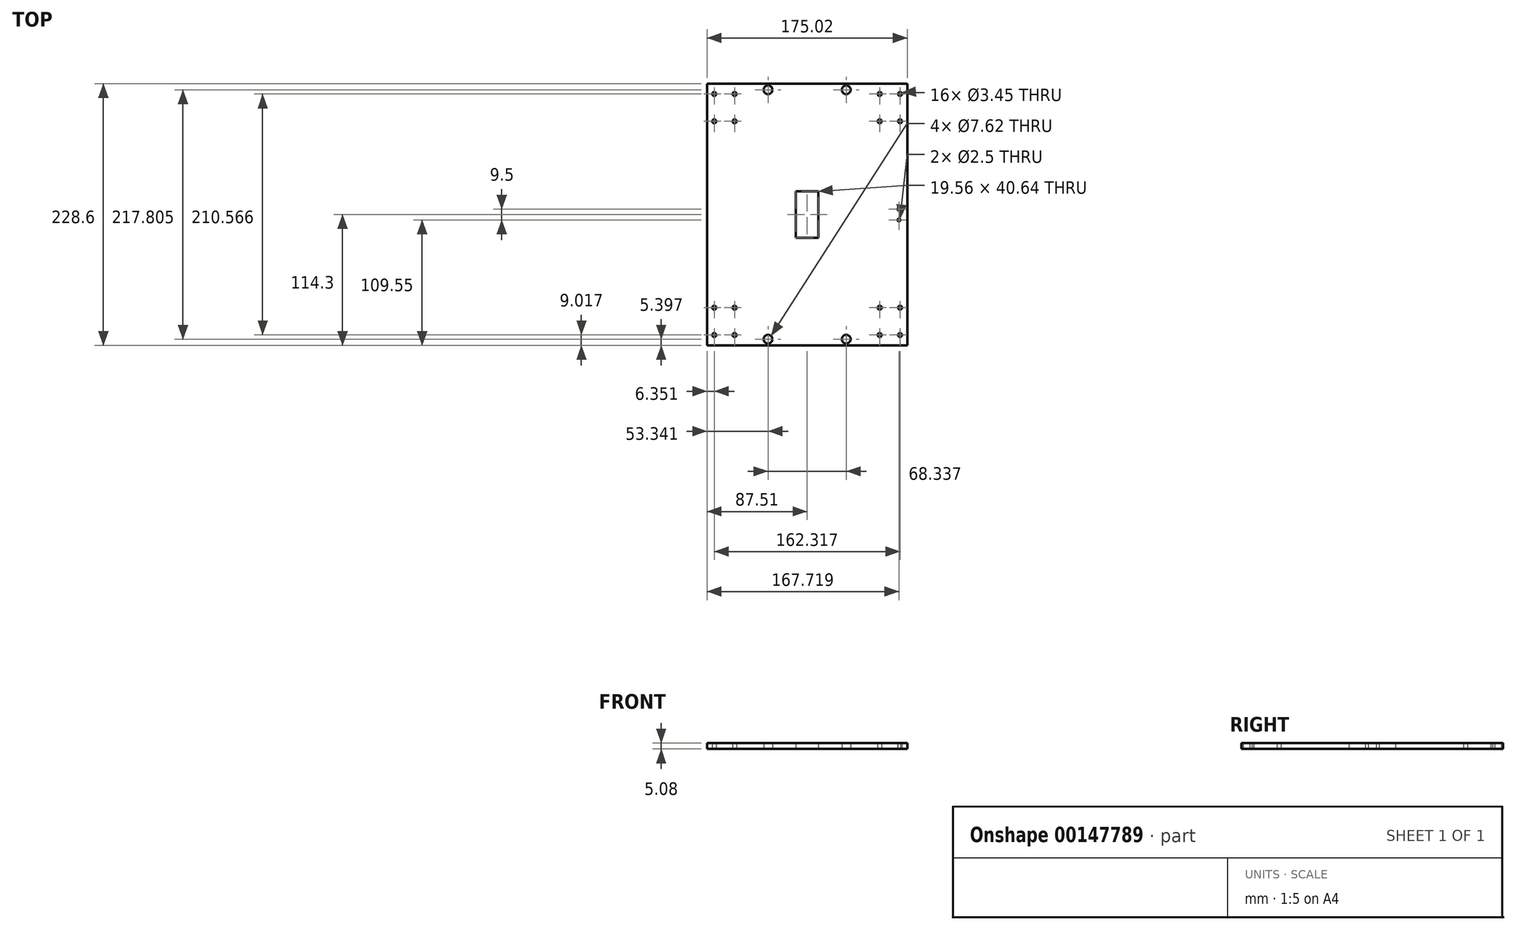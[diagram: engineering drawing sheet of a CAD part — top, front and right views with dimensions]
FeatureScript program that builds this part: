
annotation { "Feature Type Name" : "Feature", "Feature Type Description" : "" }
export const myFeature = defineFeature(function(context is Context, id is Id, definition is map)
    precondition{}
    {
        {
            var Q0;
            Q0=qCreatedBy(makeId("Top.planeOp"),FACE);
            var sketch = newSketch(context, id + "F0", { "sketchPlane" : qUnion([Q0])});
            skLineSegment(sketch, "E0.bottom", {"start": v(87.5, -114.3) * mm, "end": v(-87.5, -114.3) * mm});
            skLineSegment(sketch, "E0.top", {"start": v(87.5, 114.3) * mm, "end": v(-87.5, 114.3) * mm});
            skLineSegment(sketch, "E0.left", {"start": v(87.5, -114.3) * mm, "end": v(87.5, 114.3) * mm});
            skLineSegment(sketch, "E0.right", {"start": v(-87.5, -114.3) * mm, "end": v(-87.5, 114.3) * mm});
            skPoint(sketch, "E0.middle", {"position": v(0, 0) * mm});
            skLineSegment(sketch, "E1", {"start": v(-81.16, 114.3) * mm, "end": v(-81.16, 105.28) * mm, "construction": true});
            skLineSegment(sketch, "E2", {"start": v(-81.16, 105.28) * mm, "end": v(-87.5, 105.28) * mm, "construction": true});
            skLineSegment(sketch, "E3.bottom", {"start": v(-72.27, 93.34) * mm, "end": v(72.27, 93.34) * mm, "construction": true});
            skLineSegment(sketch, "E3.top", {"start": v(-72.27, -93.34) * mm, "end": v(72.27, -93.34) * mm, "construction": true});
            skLineSegment(sketch, "E3.left", {"start": v(-72.27, 93.34) * mm, "end": v(-72.27, -93.34) * mm, "construction": true});
            skLineSegment(sketch, "E3.right", {"start": v(72.27, 93.34) * mm, "end": v(72.27, -93.34) * mm, "construction": true});
            skLineSegment(sketch, "E4.bottom", {"start": v(-81.16, 105.28) * mm, "end": v(-63.38, 105.28) * mm, "construction": true});
            skLineSegment(sketch, "E4.top", {"start": v(-81.16, 81.4) * mm, "end": v(-63.38, 81.4) * mm, "construction": true});
            skLineSegment(sketch, "E4.left", {"start": v(-81.16, 105.28) * mm, "end": v(-81.16, 81.4) * mm, "construction": true});
            skLineSegment(sketch, "E4.right", {"start": v(-63.38, 105.28) * mm, "end": v(-63.38, 81.4) * mm, "construction": true});
            skPoint(sketch, "E4.middle", {"position": v(-72.27, 93.34) * mm});
            skLineSegment(sketch, "E5.bottom", {"start": v(81.16, 105.28) * mm, "end": v(63.38, 105.28) * mm, "construction": true});
            skLineSegment(sketch, "E5.top", {"start": v(81.16, 81.4) * mm, "end": v(63.38, 81.4) * mm, "construction": true});
            skLineSegment(sketch, "E5.left", {"start": v(81.16, 105.28) * mm, "end": v(81.16, 81.4) * mm, "construction": true});
            skLineSegment(sketch, "E5.right", {"start": v(63.38, 105.28) * mm, "end": v(63.38, 81.4) * mm, "construction": true});
            skPoint(sketch, "E5.middle", {"position": v(72.27, 93.34) * mm});
            skLineSegment(sketch, "E6.bottom", {"start": v(81.16, -105.28) * mm, "end": v(63.38, -105.28) * mm, "construction": true});
            skLineSegment(sketch, "E6.top", {"start": v(81.16, -81.4) * mm, "end": v(63.38, -81.4) * mm, "construction": true});
            skLineSegment(sketch, "E6.left", {"start": v(81.16, -105.28) * mm, "end": v(81.16, -81.4) * mm, "construction": true});
            skLineSegment(sketch, "E6.right", {"start": v(63.38, -105.28) * mm, "end": v(63.38, -81.4) * mm, "construction": true});
            skPoint(sketch, "E6.middle", {"position": v(72.27, -93.34) * mm});
            skLineSegment(sketch, "E7.bottom", {"start": v(-63.38, -105.28) * mm, "end": v(-81.16, -105.28) * mm, "construction": true});
            skLineSegment(sketch, "E7.top", {"start": v(-63.38, -81.4) * mm, "end": v(-81.16, -81.4) * mm, "construction": true});
            skLineSegment(sketch, "E7.left", {"start": v(-63.38, -105.28) * mm, "end": v(-63.38, -81.4) * mm, "construction": true});
            skLineSegment(sketch, "E7.right", {"start": v(-81.16, -105.28) * mm, "end": v(-81.16, -81.4) * mm, "construction": true});
            skPoint(sketch, "E7.middle", {"position": v(-72.27, -93.34) * mm});
            skCircle(sketch, "E8", {"center": v(-81.16, 105.28) * mm, "radius": 1.73 * mm});
            skCircle(sketch, "E9", {"center": v(-63.38, 105.28) * mm, "radius": 1.73 * mm});
            skCircle(sketch, "E10", {"center": v(-63.38, 81.4) * mm, "radius": 1.73 * mm});
            skCircle(sketch, "E11", {"center": v(-81.16, 81.4) * mm, "radius": 1.73 * mm});
            skCircle(sketch, "E12", {"center": v(81.16, 81.4) * mm, "radius": 1.73 * mm});
            skCircle(sketch, "E13", {"center": v(81.16, 105.28) * mm, "radius": 1.73 * mm});
            skCircle(sketch, "E14", {"center": v(63.38, 105.28) * mm, "radius": 1.73 * mm});
            skCircle(sketch, "E15", {"center": v(63.38, 81.4) * mm, "radius": 1.73 * mm});
            skCircle(sketch, "E16", {"center": v(81.16, -105.28) * mm, "radius": 1.73 * mm});
            skCircle(sketch, "E17", {"center": v(81.16, -81.4) * mm, "radius": 1.73 * mm});
            skCircle(sketch, "E18", {"center": v(63.38, -81.4) * mm, "radius": 1.73 * mm});
            skCircle(sketch, "E19", {"center": v(63.38, -105.28) * mm, "radius": 1.73 * mm});
            skCircle(sketch, "E20", {"center": v(-63.38, -105.28) * mm, "radius": 1.73 * mm});
            skCircle(sketch, "E21", {"center": v(-63.38, -81.4) * mm, "radius": 1.73 * mm});
            skCircle(sketch, "E22", {"center": v(-81.16, -81.4) * mm, "radius": 1.73 * mm});
            skCircle(sketch, "E23", {"center": v(-81.16, -105.28) * mm, "radius": 1.73 * mm});
            skLineSegment(sketch, "E24.bottom", {"start": v(9.78, 20.32) * mm, "end": v(-9.78, 20.32) * mm});
            skLineSegment(sketch, "E24.top", {"start": v(9.78, -20.32) * mm, "end": v(-9.78, -20.32) * mm});
            skLineSegment(sketch, "E24.left", {"start": v(9.78, 20.32) * mm, "end": v(9.78, -20.32) * mm});
            skLineSegment(sketch, "E24.right", {"start": v(-9.78, 20.32) * mm, "end": v(-9.78, -20.32) * mm});
            skLineSegment(sketch, "E25", {"start": v(87.5, 0) * mm, "end": v(80.2, 0) * mm, "construction": true});
            skLineSegment(sketch, "E26", {"start": v(80.2, 4.75) * mm, "end": v(80.2, -4.75) * mm, "construction": true});
            skCircle(sketch, "E27", {"center": v(80.2, 4.75) * mm, "radius": 1.25 * mm});
            skCircle(sketch, "E28", {"center": v(80.2, -4.75) * mm, "radius": 1.25 * mm});
            skLineSegment(sketch, "E29", {"start": v(-63.38, -105.28) * mm, "end": v(-34.17, -105.28) * mm, "construction": true});
            skLineSegment(sketch, "E30", {"start": v(-34.17, -105.28) * mm, "end": v(-34.17, -108.9) * mm, "construction": true});
            skLineSegment(sketch, "E31", {"start": v(-34.17, -108.9) * mm, "end": v(-34.17, -114.3) * mm, "construction": true});
            skCircle(sketch, "E32", {"center": v(-34.17, -108.9) * mm, "radius": 3.8 * mm});
            skLineSegment(sketch, "E33", {"start": v(63.38, -105.28) * mm, "end": v(34.17, -105.28) * mm, "construction": true});
            skLineSegment(sketch, "E34", {"start": v(34.17, -105.28) * mm, "end": v(34.17, -108.9) * mm, "construction": true});
            skLineSegment(sketch, "E35", {"start": v(-63.38, 105.28) * mm, "end": v(-34.17, 105.28) * mm, "construction": true});
            skLineSegment(sketch, "E36", {"start": v(-34.17, 105.28) * mm, "end": v(-34.17, 108.9) * mm, "construction": true});
            skLineSegment(sketch, "E37", {"start": v(63.38, 105.28) * mm, "end": v(34.17, 105.28) * mm, "construction": true});
            skLineSegment(sketch, "E38", {"start": v(34.17, 105.28) * mm, "end": v(34.17, 108.9) * mm, "construction": true});
            skCircle(sketch, "E39", {"center": v(34.17, -108.9) * mm, "radius": 3.8 * mm});
            skCircle(sketch, "E40", {"center": v(-34.17, 108.9) * mm, "radius": 3.8 * mm});
            skCircle(sketch, "E41", {"center": v(34.17, 108.9) * mm, "radius": 3.8 * mm});
            skSolve(sketch);
        }
        {
            var Q0;
            Q0=qSketchRegion(id+"F0",true);
            extrude(context, id + "F1", {"entities" : qUnion([Q0]), "depth" : 5.08 * mm});
        }
    });
